# Revit family: DOB30M977S_Revit
name_source: partatom
category: Specialty Equipment
revit_build: Autodesk Revit MEP 2014 (Build: 20130308_1515(x64)
units: mm (PartAtom-declared; Revit-internal decimal feet)

## types (1)
- DOB30M977S
    AUTO CONVERSION = YES
    AUTOMATIC WATER RESERVOIR = 1 (UPPER)
    BAKE ELEMENT = 3,000W - 8 PASS
    BROIL = 4,400W - 10 PASS
    CHILD LOCK = YES
    CIRCUIT BREAKER (A) = 50
    CLEANING TYPE = SELF CLEAN & GREENCLEAN
    CONTROLS = 7” TFT LCD
    CONVECTION ELEMENT = 1,300W (EACH - 2,600W TOTAL)
    CONVECTION TYPE = FOUR PART DUAL PURE CONVECTION WITH MESH FILTER
    COOKIE SHEETS (SET OF 3) = SKU - ACSM303
    COOKING MODES = BAKE - BROIL - CONVECTION BAKE - CONVECTION ROAST - CONVECTION BROIL - FOUR PART PURE CONVECTION - PURE CONVECTION SEAR - STEAM BAKE - STEAM ROAST
    DEHYDRATE = YES
    DELAY START = YES
    Depth = 23 1/8"
    Description = 30-INCH SINGLE WALL OVEN MODERNIST COLLECTION
    Door = Plastic-Black
    Door Glass = Glass
    ENERGY SOURCE = ELECTRIC
    FREQUENCY (HZ) = 60
    GLIDERACK™ = 2 (UPPER) / 2 (LOWER)
    GOURMET COOK = YES
    Handle = Stainless Steel
    Height = 51 1/2"
    INSTANTHEAT™ = YES
    KEEP WARM = YES
    KITCHEN TIMER = YES
    LIGHTING = BRIGHTVUE™ - LED + HALOGEN
    LIMITED, PARTS AND LABOR = 1 YEAR
    MESH FILTER = 4
    Manufacturer = Dacor
    Model = DOB30M977S
    NET WEIGHT (LBS) = 139
    PIZZA STONE MODE = YES
    PROOF = YES
    PROOF (LOWER TEMP) = YES
    RACK POSITIONS = 6
    SABBATH MODE = YES
    STANDARD RACK = 1 (UPPER) / 1 (LOWER)
    STEAM HEATER = 500W
    Support = Plastic-Black
    TEMPERATURE PROBE = YES
    Unit = Stainless Steel
    VOLTS (V) = 240 / 208
    WI FI = YES
    Width = 29 3/4"

## geometry (parser evidence)
native form markers: Blend x4, Sweep x1
no freeform markers — native parametric forms only
